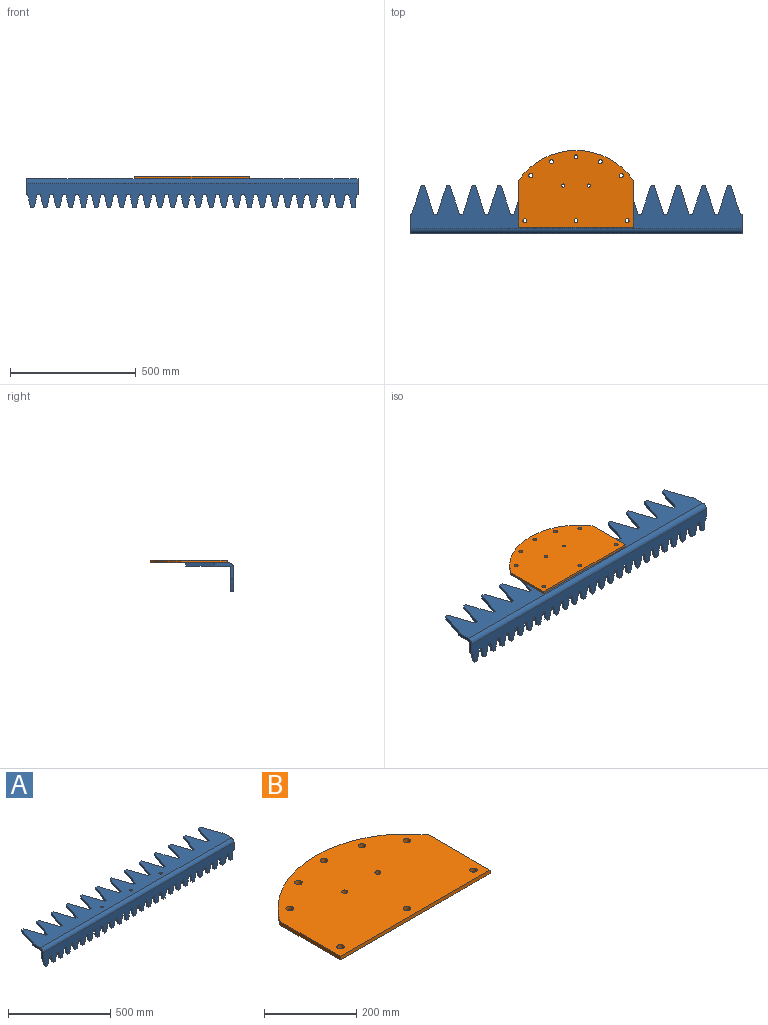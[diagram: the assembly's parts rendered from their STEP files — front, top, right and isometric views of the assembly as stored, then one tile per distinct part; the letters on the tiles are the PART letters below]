
ASSEMBLY  parts=2 mates=1
PART A: 169 faces, bbox 1320.8x190.5x114.3 mm
  f0: plane 12.7x12.7mm, normal (0,0,-1), area 161.3mm2, adj f26,f27,f130,f164
  f1: plane 12.7x12.7mm, normal (0,0,-1), area 161.3mm2, adj f26,f27,f137,f162
  f2: plane 12.7x12.7mm, normal (0,0,-1), area 161.3mm2, adj f26,f27,f159,f161
  f3: plane 12.7x12.7mm, normal (0,0,-1), area 161.3mm2, adj f26,f27,f152,f156
  f4: plane 12.7x12.7mm, normal (0,0,-1), area 161.3mm2, adj f26,f27,f153,f158
  f5: plane 12.7x12.7mm, normal (0,0,-1), area 161.3mm2, adj f26,f27,f150,f155
  f6: plane 12.7x12.7mm, normal (0,0,-1), area 161.3mm2, adj f26,f27,f143,f147
  f7: plane 12.7x12.7mm, normal (0,0,-1), area 161.3mm2, adj f26,f27,f140,f144
  f8: plane 12.7x12.7mm, normal (0,0,-1), area 161.3mm2, adj f26,f27,f87,f141
  f9: plane 12.7x12.7mm, normal (0,0,-1), area 161.3mm2, adj f26,f27,f134,f138
  f10: plane 12.7x12.7mm, normal (0,0,-1), area 161.3mm2, adj f26,f27,f135,f146
  f11: plane 12.7x12.7mm, normal (0,0,-1), area 161.3mm2, adj f26,f27,f132,f149
  f12: plane 12.7x12.7mm, normal (0,0,-1), area 161.3mm2, adj f26,f27,f122,f128
  f13: plane 12.7x12.7mm, normal (0,0,-1), area 161.3mm2, adj f26,f27,f126,f131
  f14: plane 12.7x12.7mm, normal (0,0,-1), area 161.3mm2, adj f26,f27,f123,f125
  f15: plane 12.7x12.7mm, normal (0,0,-1), area 161.3mm2, adj f26,f27,f117,f120
  f16: plane 20.23x12.7mm, normal (0,0,-1), area 256.9mm2, adj f26,f27,f115,f119
  f17: plane 12.7x12.7mm, normal (0,0,-1), area 161.3mm2, adj f26,f27,f112,f114
  f18: plane 12.7x12.7mm, normal (0,0,-1), area 161.3mm2, adj f26,f27,f109,f111
  f19: plane 12.7x12.7mm, normal (0,0,-1), area 161.3mm2, adj f26,f27,f106,f108
  f20: plane 12.7x12.7mm, normal (0,0,-1), area 161.3mm2, adj f26,f27,f103,f105
  f21: plane 12.7x12.7mm, normal (0,0,-1), area 161.3mm2, adj f26,f27,f100,f102
  f22: plane 12.7x12.7mm, normal (0,0,-1), area 161.3mm2, adj f26,f27,f97,f99
  f23: plane 12.7x12.7mm, normal (0,0,-1), area 161.3mm2, adj f26,f27,f94,f96
  f24: plane 12.7x12.7mm, normal (0,0,-1), area 161.3mm2, adj f26,f27,f91,f93
  f25: plane 12.7x12.7mm, normal (0,0,-1), area 161.3mm2, adj f26,f27,f88,f90
  f26: plane 1320.8x95.25mm, normal (0,-1,0), area 92449.2mm2, adj f0,f1,f2,f3,f4,f5,f6,f7
  f27: plane 1320.8x95.25mm, normal (0,1,0), area 92449.2mm2, adj f0,f1,f2,f3,f4,f5,f6,f7
  f28: plane 12.7x12.7mm, normal (0,1,0), area 161.3mm2, adj f43,f45,f84,f86
  f29: plane 12.7x12.7mm, normal (0,1,0), area 161.3mm2, adj f43,f45,f81,f83
  f30: plane 12.7x12.7mm, normal (0,1,0), area 161.3mm2, adj f43,f45,f78,f80
  f31: plane 12.7x12.7mm, normal (0,1,0), area 161.3mm2, adj f43,f45,f75,f77
  f32: plane 12.7x12.7mm, normal (0,1,0), area 161.3mm2, adj f43,f45,f72,f74
  f33: plane 12.7x12.7mm, normal (0,1,0), area 161.3mm2, adj f43,f45,f69,f71
  f34: plane 12.7x12.7mm, normal (0,1,0), area 161.3mm2, adj f43,f45,f66,f68
  f35: plane 12.7x12.7mm, normal (0,1,0), area 161.3mm2, adj f43,f45,f63,f65
  f36: plane 12.7x12.7mm, normal (0,1,0), area 161.3mm2, adj f43,f45,f60,f62
  f37: plane 12.7x12.7mm, normal (0,1,0), area 161.3mm2, adj f43,f45,f57,f59
  f38: plane 12.7x12.7mm, normal (0,1,0), area 161.3mm2, adj f43,f45,f54,f56
  f39: plane 12.7x12.7mm, normal (0,1,0), area 161.3mm2, adj f43,f45,f51,f53
  f40: plane 12.7x12.7mm, normal (0,1,0), area 161.3mm2, adj f43,f45,f47,f50
  f41: plane 76.2x63.5mm, normal (-1,0,0), area 1543.7mm2, adj f26,f27,f43,f44,f45,f46,f85,f165
  f42: plane 76.2x63.5mm, normal (1,0,0), area 1543.7mm2, adj f26,f27,f43,f44,f45,f46,f48,f121
  f43: plane 1320.8x171.45mm, normal (0,0,1), area 150373.6mm2, adj f28,f29,f30,f31,f32,f33,f34,f35
  f44: cylinder r=6.35mm len=1320.8mm, axis (-1,0,0), area 13174.4mm2, adj f27,f41,f42,f45
  f45: plane 1320.8x171.45mm, normal (0,0,-1), area 150373.6mm2, adj f28,f29,f30,f31,f32,f33,f34,f35
  f46: cylinder r=19.05mm len=1320.8mm, axis (1,0,0), area 39523.2mm2, adj f26,f41,f42,f43
  f47: plane 114.3x38.1mm, normal (0.95,0.32,0), area 1530.1mm2, adj f40,f43,f45,f48
  f48: plane 12.7x6.35mm, normal (0,1,0), area 80.6mm2, adj f42,f43,f45,f47
  f49: plane 12.7x12.7mm, normal (0,1,0), area 161.3mm2, adj f43,f45,f50,f51
  f50: plane 114.3x38.1mm, normal (-0.95,0.32,0), area 1530.1mm2, adj f40,f43,f45,f49
  f51: plane 114.3x38.1mm, normal (0.95,0.32,0), area 1530.1mm2, adj f39,f43,f45,f49
  f52: plane 12.7x12.7mm, normal (0,1,0), area 161.3mm2, adj f43,f45,f53,f54
  f53: plane 114.3x38.1mm, normal (-0.95,0.32,0), area 1530.1mm2, adj f39,f43,f45,f52
  f54: plane 114.3x38.1mm, normal (0.95,0.32,0), area 1530.1mm2, adj f38,f43,f45,f52
  f55: plane 12.7x12.7mm, normal (0,1,0), area 161.3mm2, adj f43,f45,f56,f57
  f56: plane 114.3x38.1mm, normal (-0.95,0.32,0), area 1530.1mm2, adj f38,f43,f45,f55
  f57: plane 114.3x38.1mm, normal (0.95,0.32,0), area 1530.1mm2, adj f37,f43,f45,f55
  f58: plane 12.7x12.7mm, normal (0,1,0), area 161.3mm2, adj f43,f45,f59,f60
  f59: plane 114.3x38.1mm, normal (-0.95,0.32,0), area 1530.1mm2, adj f37,f43,f45,f58
  f60: plane 114.3x38.1mm, normal (0.95,0.32,0), area 1530.1mm2, adj f36,f43,f45,f58
  f61: plane 12.7x12.7mm, normal (0,1,0), area 161.3mm2, adj f43,f45,f62,f63
  f62: plane 114.3x38.1mm, normal (-0.95,0.32,0), area 1530.1mm2, adj f36,f43,f45,f61
  f63: plane 114.3x38.1mm, normal (0.95,0.32,0), area 1530.1mm2, adj f35,f43,f45,f61
  f64: plane 12.7x12.7mm, normal (0,1,0), area 161.3mm2, adj f43,f45,f65,f66
  f65: plane 114.3x38.1mm, normal (-0.95,0.32,0), area 1530.1mm2, adj f35,f43,f45,f64
  f66: plane 114.3x38.1mm, normal (0.95,0.32,0), area 1530.1mm2, adj f34,f43,f45,f64
  f67: plane 12.7x12.7mm, normal (0,1,0), area 161.3mm2, adj f43,f45,f68,f69
  f68: plane 114.3x38.1mm, normal (-0.95,0.32,0), area 1530.1mm2, adj f34,f43,f45,f67
  f69: plane 114.3x38.1mm, normal (0.95,0.32,0), area 1530.1mm2, adj f33,f43,f45,f67
  f70: plane 12.7x12.7mm, normal (0,1,0), area 161.3mm2, adj f43,f45,f71,f72
  f71: plane 114.3x38.1mm, normal (-0.95,0.32,0), area 1530.1mm2, adj f33,f43,f45,f70
  f72: plane 114.3x38.1mm, normal (0.95,0.32,0), area 1530.1mm2, adj f32,f43,f45,f70
  f73: plane 12.7x12.7mm, normal (0,1,0), area 161.3mm2, adj f43,f45,f74,f75
  f74: plane 114.3x38.1mm, normal (-0.95,0.32,0), area 1530.1mm2, adj f32,f43,f45,f73
  f75: plane 114.3x38.1mm, normal (0.95,0.32,0), area 1530.1mm2, adj f31,f43,f45,f73
  f76: plane 12.7x12.7mm, normal (0,1,0), area 161.3mm2, adj f43,f45,f77,f78
  f77: plane 114.3x38.1mm, normal (-0.95,0.32,0), area 1530.1mm2, adj f31,f43,f45,f76
  f78: plane 114.3x38.1mm, normal (0.95,0.32,0), area 1530.1mm2, adj f30,f43,f45,f76
  f79: plane 12.7x12.7mm, normal (0,1,0), area 161.3mm2, adj f43,f45,f80,f81
  f80: plane 114.3x38.1mm, normal (-0.95,0.32,0), area 1530.1mm2, adj f30,f43,f45,f79
  f81: plane 114.3x38.1mm, normal (0.95,0.32,0), area 1530.1mm2, adj f29,f43,f45,f79
  f82: plane 12.7x12.7mm, normal (0,1,0), area 161.3mm2, adj f43,f45,f83,f84
  f83: plane 114.3x38.1mm, normal (-0.95,0.32,0), area 1530.1mm2, adj f29,f43,f45,f82
  f84: plane 114.3x38.1mm, normal (0.95,0.32,0), area 1530.1mm2, adj f28,f43,f45,f82
  f85: plane 12.7x6.35mm, normal (0,1,0), area 80.6mm2, adj f41,f43,f45,f86
  f86: plane 114.3x38.1mm, normal (-0.95,0.32,0), area 1530.1mm2, adj f28,f43,f45,f85
  f87: plane 50.8x12.7mm, normal (0.97,0,-0.24), area 665mm2, adj f8,f26,f27,f89
  f88: plane 50.8x12.7mm, normal (-0.97,0,-0.24), area 665mm2, adj f25,f26,f27,f89
  f89: plane 12.7x12.7mm, normal (0,0,-1), area 161.3mm2, adj f26,f27,f87,f88
  f90: plane 50.8x12.7mm, normal (0.97,0,-0.24), area 665mm2, adj f25,f26,f27,f92
  f91: plane 50.8x12.7mm, normal (-0.97,0,-0.24), area 665mm2, adj f24,f26,f27,f92
  f92: plane 12.7x12.7mm, normal (0,0,-1), area 161.3mm2, adj f26,f27,f90,f91
  f93: plane 50.8x12.7mm, normal (0.97,0,-0.24), area 665mm2, adj f24,f26,f27,f95
  f94: plane 50.8x12.7mm, normal (-0.97,0,-0.24), area 665mm2, adj f23,f26,f27,f95
  f95: plane 12.7x12.7mm, normal (0,0,-1), area 161.3mm2, adj f26,f27,f93,f94
  f96: plane 50.8x12.7mm, normal (0.97,0,-0.24), area 665mm2, adj f23,f26,f27,f98
  f97: plane 50.8x12.7mm, normal (-0.97,0,-0.24), area 665mm2, adj f22,f26,f27,f98
  f98: plane 12.7x12.7mm, normal (0,0,-1), area 161.3mm2, adj f26,f27,f96,f97
  f99: plane 50.8x12.7mm, normal (0.97,0,-0.24), area 665mm2, adj f22,f26,f27,f101
  f100: plane 50.8x12.7mm, normal (-0.97,0,-0.24), area 665mm2, adj f21,f26,f27,f101
  f101: plane 12.7x12.7mm, normal (0,0,-1), area 161.3mm2, adj f26,f27,f99,f100
  f102: plane 50.8x12.7mm, normal (0.97,0,-0.24), area 665mm2, adj f21,f26,f27,f104
  f103: plane 50.8x12.7mm, normal (-0.97,0,-0.24), area 665mm2, adj f20,f26,f27,f104
  f104: plane 12.7x12.7mm, normal (0,0,-1), area 161.3mm2, adj f26,f27,f102,f103
  f105: plane 50.8x12.7mm, normal (0.97,0,-0.24), area 665mm2, adj f20,f26,f27,f107
  f106: plane 50.8x12.7mm, normal (-0.97,0,-0.24), area 665mm2, adj f19,f26,f27,f107
  f107: plane 12.7x12.7mm, normal (0,0,-1), area 161.3mm2, adj f26,f27,f105,f106
  f108: plane 50.8x12.7mm, normal (0.97,0,-0.24), area 665mm2, adj f19,f26,f27,f110
  f109: plane 50.8x12.7mm, normal (-0.97,0,-0.24), area 665mm2, adj f18,f26,f27,f110
  f110: plane 12.7x12.7mm, normal (0,0,-1), area 161.3mm2, adj f26,f27,f108,f109
  f111: plane 50.8x12.7mm, normal (0.97,0,-0.24), area 665mm2, adj f18,f26,f27,f113
  f112: plane 50.8x12.7mm, normal (-0.97,0,-0.24), area 665mm2, adj f17,f26,f27,f113
  f113: plane 12.7x12.7mm, normal (0,0,-1), area 161.3mm2, adj f26,f27,f111,f112
  f114: plane 50.8x12.7mm, normal (0.97,0,-0.24), area 665mm2, adj f17,f26,f27,f116
  f115: plane 50.8x12.7mm, normal (-0.97,0,-0.24), area 665mm2, adj f16,f26,f27,f116
  f116: plane 12.7x12.7mm, normal (0,0,-1), area 161.3mm2, adj f26,f27,f114,f115
  f117: plane 50.8x12.7mm, normal (-0.97,0,-0.24), area 665mm2, adj f15,f26,f27,f118
  f118: plane 12.7x12.7mm, normal (0,0,-1), area 161.3mm2, adj f26,f27,f117,f119
  f119: plane 50.8x12.7mm, normal (0.97,0,-0.24), area 665mm2, adj f16,f26,f27,f118
  f120: plane 50.8x12.7mm, normal (0.99,0,-0.1), area 648.5mm2, adj f15,f26,f27,f121
  f121: plane 12.7x6.35mm, normal (0,0,-1), area 80.6mm2, adj f26,f27,f42,f120
  f122: plane 50.8x12.7mm, normal (0.97,0,-0.24), area 665mm2, adj f12,f26,f27,f124
  f123: plane 50.8x12.7mm, normal (-0.97,0,-0.24), area 665mm2, adj f14,f26,f27,f124
  f124: plane 12.7x12.7mm, normal (0,0,-1), area 161.3mm2, adj f26,f27,f122,f123
  f125: plane 50.8x12.7mm, normal (0.97,0,-0.24), area 665mm2, adj f14,f26,f27,f127
  f126: plane 50.8x12.7mm, normal (-0.97,0,-0.24), area 665mm2, adj f13,f26,f27,f127
  f127: plane 12.7x12.7mm, normal (0,0,-1), area 161.3mm2, adj f26,f27,f125,f126
  f128: plane 50.8x12.7mm, normal (-0.97,0,-0.24), area 665mm2, adj f12,f26,f27,f129
  f129: plane 12.7x12.7mm, normal (0,0,-1), area 161.3mm2, adj f26,f27,f128,f130
  f130: plane 50.8x12.7mm, normal (0.97,0,-0.24), area 665mm2, adj f0,f26,f27,f129
  f131: plane 50.8x12.7mm, normal (0.97,0,-0.24), area 665mm2, adj f13,f26,f27,f133
  f132: plane 50.8x12.7mm, normal (-0.97,0,-0.24), area 665mm2, adj f11,f26,f27,f133
  f133: plane 12.7x12.7mm, normal (0,0,-1), area 161.3mm2, adj f26,f27,f131,f132
  f134: plane 50.8x12.7mm, normal (0.97,0,-0.24), area 665mm2, adj f9,f26,f27,f136
  f135: plane 50.8x12.7mm, normal (-0.97,0,-0.24), area 665mm2, adj f10,f26,f27,f136
  f136: plane 12.7x12.7mm, normal (0,0,-1), area 161.3mm2, adj f26,f27,f134,f135
  f137: plane 50.8x12.7mm, normal (0.97,0,-0.24), area 665mm2, adj f1,f26,f27,f139
  f138: plane 50.8x12.7mm, normal (-0.97,0,-0.24), area 665mm2, adj f9,f26,f27,f139
  f139: plane 12.7x12.7mm, normal (0,0,-1), area 161.3mm2, adj f26,f27,f137,f138
  f140: plane 50.8x12.7mm, normal (0.97,0,-0.24), area 665mm2, adj f7,f26,f27,f142
  f141: plane 50.8x12.7mm, normal (-0.97,0,-0.24), area 665mm2, adj f8,f26,f27,f142
  f142: plane 12.7x12.7mm, normal (0,0,-1), area 161.3mm2, adj f26,f27,f140,f141
  f143: plane 50.8x12.7mm, normal (0.97,0,-0.24), area 665mm2, adj f6,f26,f27,f145
  f144: plane 50.8x12.7mm, normal (-0.97,0,-0.24), area 665mm2, adj f7,f26,f27,f145
  f145: plane 12.7x12.7mm, normal (0,0,-1), area 161.3mm2, adj f26,f27,f143,f144
  f146: plane 50.8x12.7mm, normal (0.97,0,-0.24), area 665mm2, adj f10,f26,f27,f148
  f147: plane 50.8x12.7mm, normal (-0.97,0,-0.24), area 665mm2, adj f6,f26,f27,f148
  f148: plane 12.7x12.7mm, normal (0,0,-1), area 161.3mm2, adj f26,f27,f146,f147
  f149: plane 50.8x12.7mm, normal (0.97,0,-0.24), area 665mm2, adj f11,f26,f27,f151
  f150: plane 50.8x12.7mm, normal (-0.97,0,-0.24), area 665mm2, adj f5,f26,f27,f151
  f151: plane 12.7x12.7mm, normal (0,0,-1), area 161.3mm2, adj f26,f27,f149,f150
  f152: plane 50.8x12.7mm, normal (0.97,0,-0.24), area 665mm2, adj f3,f26,f27,f154
  f153: plane 50.8x12.7mm, normal (-0.97,0,-0.24), area 665mm2, adj f4,f26,f27,f154
  f154: plane 12.7x12.7mm, normal (0,0,-1), area 161.3mm2, adj f26,f27,f152,f153
  f155: plane 50.8x12.7mm, normal (0.97,0,-0.24), area 665mm2, adj f5,f26,f27,f157
  f156: plane 50.8x12.7mm, normal (-0.97,0,-0.24), area 665mm2, adj f3,f26,f27,f157
  f157: plane 12.7x12.7mm, normal (0,0,-1), area 161.3mm2, adj f26,f27,f155,f156
  f158: plane 50.8x12.7mm, normal (0.97,0,-0.24), area 665mm2, adj f4,f26,f27,f160
  f159: plane 50.8x12.7mm, normal (-0.97,0,-0.24), area 665mm2, adj f2,f26,f27,f160
  f160: plane 12.7x12.7mm, normal (0,0,-1), area 161.3mm2, adj f26,f27,f158,f159
  f161: plane 50.8x12.7mm, normal (0.97,0,-0.24), area 665mm2, adj f2,f26,f27,f163
  f162: plane 50.8x12.7mm, normal (-0.97,0,-0.24), area 665mm2, adj f1,f26,f27,f163
  f163: plane 12.7x12.7mm, normal (0,0,-1), area 161.3mm2, adj f26,f27,f161,f162
  f164: plane 50.8x12.7mm, normal (-0.97,0,-0.24), area 665mm2, adj f0,f26,f27,f165
  f165: plane 12.7x6.35mm, normal (0,0,-1), area 80.6mm2, adj f26,f27,f41,f164
  f166: cylinder r=7.94mm len=15.88mm, axis (0,0,1), area 633.4mm2, adj f43,f45
  f167: cylinder r=7.94mm len=15.88mm, axis (0,0,1), area 633.4mm2, adj f43,f45
  f168: cylinder r=7.94mm len=15.88mm, axis (0,0,1), area 633.4mm2, adj f43,f45
PART B: 16 faces, bbox 457.2x304.8x9.5 mm
  f0: plane 186.04x9.53mm, normal (-1,0,0), area 1772.1mm2, adj f1,f11,f12,f13
  f1: plane 457.2x9.53mm, normal (0,-1,0), area 4354.8mm2, adj f0,f2,f12,f13
  f2: plane 186.04x9.53mm, normal (1,0,0), area 1772.1mm2, adj f1,f11,f12,f13
  f3: cylinder r=7.94mm len=15.88mm, axis (0,0,1), area 475mm2, adj f12,f13
  f4: cylinder r=7.94mm len=15.88mm, axis (0,0,1), area 475mm2, adj f12,f13
  f5: cylinder r=7.94mm len=15.88mm, axis (0,0,1), area 475mm2, adj f12,f13
  f6: cylinder r=7.94mm len=15.88mm, axis (0,0,1), area 475mm2, adj f12,f13
  f7: cylinder r=7.94mm len=15.88mm, axis (0,0,1), area 475mm2, adj f12,f13
  f8: cylinder r=7.94mm len=15.88mm, axis (0,0,1), area 475mm2, adj f12,f13
  f9: cylinder r=7.94mm len=15.88mm, axis (0,0,1), area 475mm2, adj f12,f13
  f10: cylinder r=7.94mm len=15.88mm, axis (0,0,1), area 475mm2, adj f12,f13
  f11: cylinder r=279.4mm len=457.2mm, axis (0,0,1), area 5100.3mm2, adj f0,f2,f12,f13
  f12: plane 457.2x304.8mm, normal (0,0,-1), area 121303.7mm2, adj f0,f1,f2,f3,f4,f5,f6,f7
  f13: plane 457.2x304.8mm, normal (0,0,1), area 121303.7mm2, adj f0,f1,f2,f3,f4,f5,f6,f7
  f14: cylinder r=6.35mm len=12.7mm, axis (0,0,-1), area 380mm2, adj f12,f13
  f15: cylinder r=6.35mm len=12.7mm, axis (0,0,-1), area 380mm2, adj f12,f13
PLACE A t=(0,0,-9.52)mm
PLACE B rot(axis=(0,1,0),180deg) t=(0,82.55,-9.52)mm
MATE planar B.f11 <-> A.f167  axis (0,0,1) through (0,-44.45,0)mm
